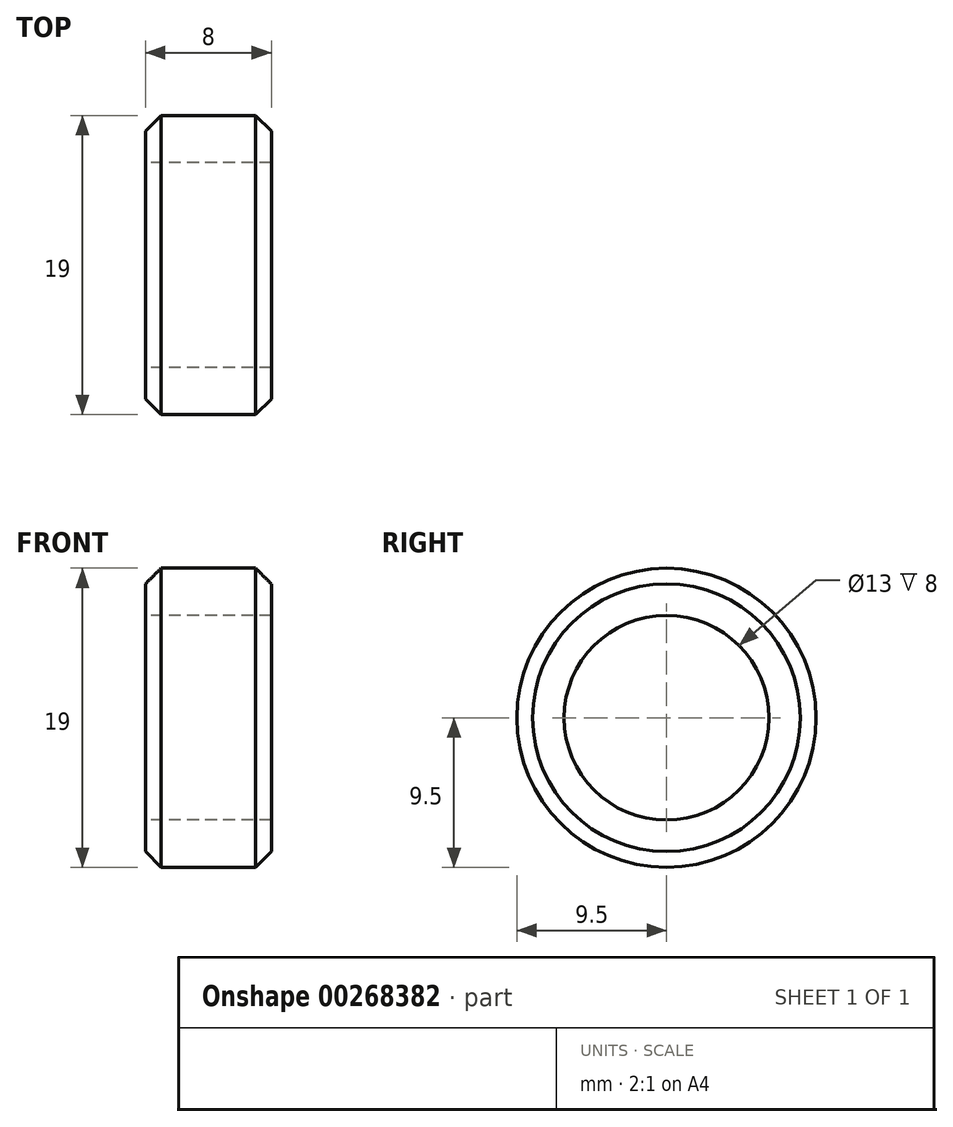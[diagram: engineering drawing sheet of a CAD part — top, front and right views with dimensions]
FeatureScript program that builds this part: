
annotation { "Feature Type Name" : "Feature", "Feature Type Description" : "" }
export const myFeature = defineFeature(function(context is Context, id is Id, definition is map)
    precondition{}
    {
        {
            var Q0;
            Q0=qCreatedBy(makeId("Top.planeOp"),FACE);
            var sketch = newSketch(context, id + "F0", { "sketchPlane" : qUnion([Q0])});
            skLineSegment(sketch, "E0.bottom", {"start": v(4, -1.5) * mm, "end": v(-4, -1.5) * mm});
            skLineSegment(sketch, "E0.top", {"start": v(4, 1.5) * mm, "end": v(-4, 1.5) * mm});
            skLineSegment(sketch, "E0.left", {"start": v(4, -1.5) * mm, "end": v(4, 1.5) * mm});
            skLineSegment(sketch, "E0.right", {"start": v(-4, -1.5) * mm, "end": v(-4, 1.5) * mm});
            skPoint(sketch, "E0.middle", {"position": v(0, 0) * mm});
            skLineSegment(sketch, "E1", {"start": v(-4, 0.5) * mm, "end": v(-3, 1.5) * mm});
            skLineSegment(sketch, "E2.MirrorCS", {"start": v(4, 0.5) * mm, "end": v(3, 1.5) * mm});
            skLineSegment(sketch, "E3.bottom", {"start": v(-4, -1.5) * mm, "end": v(4, -1.5) * mm, "construction": true});
            skLineSegment(sketch, "E3.top", {"start": v(-4, -8) * mm, "end": v(4, -8) * mm, "construction": true});
            skLineSegment(sketch, "E3.left", {"start": v(-4, -1.5) * mm, "end": v(-4, -8) * mm, "construction": true});
            skLineSegment(sketch, "E3.right", {"start": v(4, -1.5) * mm, "end": v(4, -8) * mm, "construction": true});
            skSolve(sketch);
        }
        {
            var Q0;
            {var subQ1=sQuery(id+"F0.wireOp",EDGE,"E0.bottom");Q0=makeQuery(id+"F0.imprint","IMPRINT",FACE,{"disambiguationData":[TD([[makeQuery(id+"F0.imprint","IMPRINT",EDGE,{"derivedFrom":subQ1}),-1.0]])]});}
            var Q1;
            Q1=sQuery(id+"F0.wireOp",EDGE,"E3.top");
            revolve(context, id + "F1", {"entities" : qUnion([Q0]), "axis" : qUnion([Q1]), "revolveType" : RevolveType.FULL});
        }
    });
